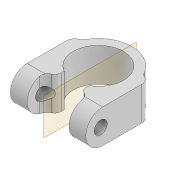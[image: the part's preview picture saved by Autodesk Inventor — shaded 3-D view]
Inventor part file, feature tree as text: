
AUTODESK INVENTOR PART (.ipt)
format: ipt  version: 2022 (Build 260153000, 153)  size: 216,064 bytes
history: native  units: mm
features: fillet x4, extrude x3, sketch x3, projected_geometry x3, thicken_offset x2, mirror x1
ambient origin geometry x8: Origin, YZ Plane, XZ Plane, XY Plane, X Axis, Y Axis, Z Axis, Center Point
bodies: Solid1 (feature_tree)
feature tree (16):
  extrude  "Extrusion1"  Depth=2.0mm
  fillet  "Fillet1"  Radius=4.0mm
  extrude  "Extrusion2"  Depth=3.0mm
  extrude  "Extrusion3"  Depth=2.0mm
  fillet  "Fillet2"  Radius=3.1mm
  mirror  "Mirror1"
  fillet  "Fillet7"  Radius=2.0mm
  thicken_offset  "Thicken1"
  thicken_offset  "Thicken2"
  fillet  "Fillet8"  Radius=100.0mm
  sketch  "Sketch1"  dims[d0=12.0mm d1=2.0mm d3=4.0mm]
  sketch  "Sketch2"  dims[d4=3.0mm d5=3.0mm]
  projected_geometry  "Projected Loop1"
  sketch  "Sketch4"  dims[d6=8.0mm d7=0.0mm d8=1.5mm d9=3.1mm d10=2.0mm d12=100.0mm d13=0.0mm d14=2.0mm d15=0.0mm d16=2.0mm d22=3.0mm d28=4.0mm d47=4.0mm d48=1.0mm d49=1.0mm d50=1.0mm d51=1.0mm d52=2.0mm d29=0.872665mm d30=0.5mm d31=0.872665mm d32=0.0mm]
  projected_geometry  "Projected Loop2"
  projected_geometry  "Projected Loop4"
